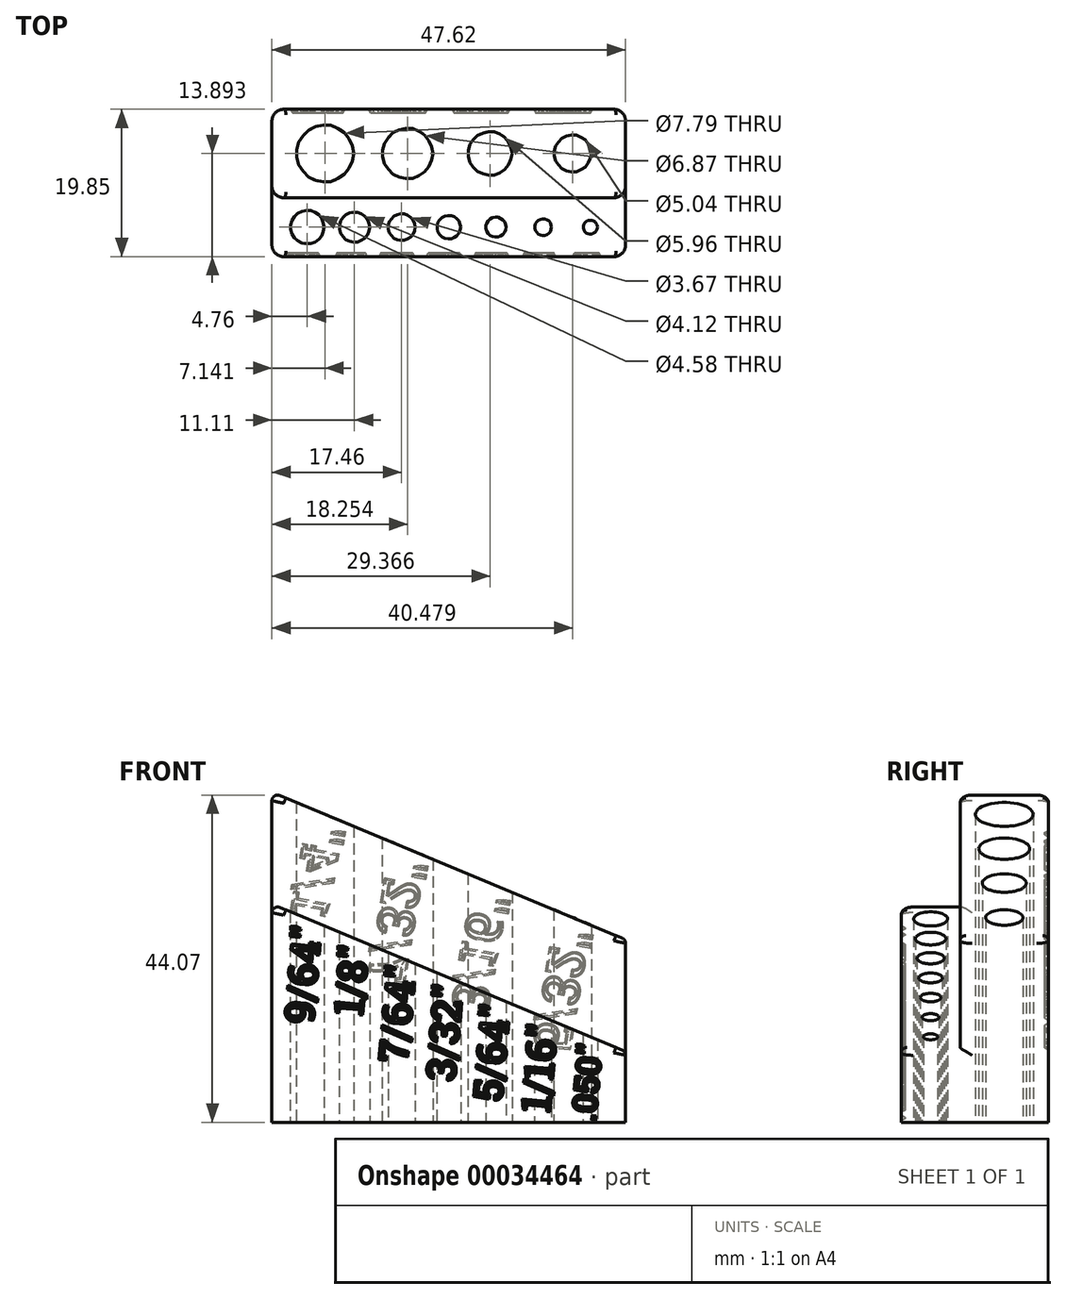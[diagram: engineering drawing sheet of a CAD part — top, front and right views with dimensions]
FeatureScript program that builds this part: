
annotation { "Feature Type Name" : "Feature", "Feature Type Description" : "" }
export const myFeature = defineFeature(function(context is Context, id is Id, definition is map)
    precondition{}
    {
        {
            var Q0;
            Q0=qCreatedBy(makeId("Front.planeOp"),FACE);
            var sketch = newSketch(context, id + "F0", { "sketchPlane" : qUnion([Q0])});
            skLineSegment(sketch, "E0", {"start": v(-23.81, 0) * mm, "end": v(23.81, 0) * mm});
            skLineSegment(sketch, "E1", {"start": v(23.81, 0) * mm, "end": v(23.81, 9.53) * mm});
            skLineSegment(sketch, "E2", {"start": v(23.81, 9.53) * mm, "end": v(-23.81, 29.37) * mm});
            skLineSegment(sketch, "E3", {"start": v(-23.81, 29.37) * mm, "end": v(-23.81, 0) * mm});
            skLineSegment(sketch, "E4", {"start": v(0, 0) * mm, "end": v(0, 19.45) * mm, "construction": true});
            skSolve(sketch);
        }
        {
            var Q0;
            Q0 = qSketchRegion(id + "F0", true);
            extrude(context, id + "F1", {"entities" : qUnion([Q0]), "depth" : 7.94 * mm});
        }
        {
            var Q0;
            Q0=qCreatedBy(makeId("Front.planeOp"),FACE);
            var sketch = newSketch(context, id + "F2", { "sketchPlane" : qUnion([Q0])});
            skLineSegment(sketch, "E5.0", {"start": v(-23.81, 0) * mm, "end": v(23.81, 0) * mm});
            skLineSegment(sketch, "E6", {"start": v(23.81, 0) * mm, "end": v(23.81, 24.6) * mm});
            skLineSegment(sketch, "E7", {"start": v(-23.81, 0) * mm, "end": v(-23.81, 44.45) * mm});
            skLineSegment(sketch, "E8", {"start": v(-23.81, 44.45) * mm, "end": v(23.81, 24.6) * mm});
            skLineSegment(sketch, "E9.0", {"start": v(23.81, 9.52) * mm, "end": v(-23.81, 29.37) * mm, "construction": true});
            skSolve(sketch);
        }
        {
            var Q0;
            Q0 = qSketchRegion(id + "F2", true);
            extrude(context, id + "F3", {"entities" : qUnion([Q0]), "operationType" : NewBodyOperationType.ADD, "oppositeDirection" : true, "depth" : 11.9 * mm});
        }
        {
            var Q0;
            Q0=qCreatedBy(makeId("Top.planeOp"),FACE);
            var sketch = newSketch(context, id + "F4", { "sketchPlane" : qUnion([Q0])});
            skLineSegment(sketch, "E10.0", {"start": v(23.81, 0) * mm, "end": v(-23.81, 0) * mm, "construction": true});
            skLineSegment(sketch, "E11.bottom", {"start": v(23.81, -7.94) * mm, "end": v(-23.81, -7.94) * mm, "construction": true});
            skLineSegment(sketch, "E11.top", {"start": v(23.81, 11.9) * mm, "end": v(-23.81, 11.9) * mm, "construction": true});
            skLineSegment(sketch, "E12", {"start": v(23.81, -3.97) * mm, "end": v(-23.81, -3.97) * mm, "construction": true});
            skLineSegment(sketch, "E13", {"start": v(23.81, -7.94) * mm, "end": v(23.81, 0) * mm, "construction": true});
            skLineSegment(sketch, "E14", {"start": v(-23.81, -7.94) * mm, "end": v(-23.81, 0) * mm, "construction": true});
            skLineSegment(sketch, "E15", {"start": v(-23.81, 11.9) * mm, "end": v(-23.81, 0) * mm, "construction": true});
            skLineSegment(sketch, "E16", {"start": v(23.81, 0) * mm, "end": v(23.81, 11.9) * mm, "construction": true});
            skCircle(sketch, "E17", {"center": v(19.05, -3.97) * mm, "radius": 0.73 * mm, "construction": true});
            skLineSegment(sketch, "E18", {"start": v(19.68, -4.34) * mm, "end": v(19.68, -3.6) * mm, "construction": true});
            skLineSegment(sketch, "E19", {"start": v(19.68, -3.6) * mm, "end": v(19.05, -3.24) * mm, "construction": true});
            skLineSegment(sketch, "E20", {"start": v(18.41, -4.34) * mm, "end": v(19.05, -4.7) * mm, "construction": true});
            skLineSegment(sketch, "E21", {"start": v(19.05, -4.7) * mm, "end": v(19.68, -4.34) * mm, "construction": true});
            skLineSegment(sketch, "E22", {"start": v(18.41, -4.34) * mm, "end": v(18.41, -3.6) * mm, "construction": true});
            skLineSegment(sketch, "E23", {"start": v(18.41, -3.6) * mm, "end": v(19.05, -3.24) * mm, "construction": true});
            skCircle(sketch, "E24", {"center": v(19.05, -3.97) * mm, "radius": 0.96 * mm});
            skLineSegment(sketch, "E25", {"start": v(19.05, -4.7) * mm, "end": v(19.05, -4.93) * mm, "construction": true});
            skCircle(sketch, "E26", {"center": v(12.7, -3.97) * mm, "radius": 0.92 * mm, "construction": true});
            skLineSegment(sketch, "E27", {"start": v(13.5, -4.43) * mm, "end": v(13.5, -3.51) * mm, "construction": true});
            skLineSegment(sketch, "E28", {"start": v(13.5, -3.51) * mm, "end": v(12.7, -3.05) * mm, "construction": true});
            skLineSegment(sketch, "E29", {"start": v(11.9, -4.43) * mm, "end": v(12.7, -4.89) * mm, "construction": true});
            skLineSegment(sketch, "E30", {"start": v(12.7, -4.89) * mm, "end": v(13.5, -4.43) * mm, "construction": true});
            skLineSegment(sketch, "E31", {"start": v(11.9, -4.43) * mm, "end": v(11.9, -3.51) * mm, "construction": true});
            skLineSegment(sketch, "E32", {"start": v(11.9, -3.51) * mm, "end": v(12.7, -3.05) * mm, "construction": true});
            skCircle(sketch, "E33", {"center": v(12.7, -3.97) * mm, "radius": 1.15 * mm});
            skLineSegment(sketch, "E34", {"start": v(12.7, -4.89) * mm, "end": v(12.7, -5.11) * mm, "construction": true});
            skCircle(sketch, "E35", {"center": v(6.35, -3.97) * mm, "radius": 1.15 * mm, "construction": true});
            skLineSegment(sketch, "E36", {"start": v(7.34, -4.54) * mm, "end": v(7.34, -3.4) * mm, "construction": true});
            skLineSegment(sketch, "E37", {"start": v(7.34, -3.4) * mm, "end": v(6.35, -2.82) * mm, "construction": true});
            skLineSegment(sketch, "E38", {"start": v(5.36, -4.54) * mm, "end": v(6.35, -5.11) * mm, "construction": true});
            skLineSegment(sketch, "E39", {"start": v(6.35, -5.11) * mm, "end": v(7.34, -4.54) * mm, "construction": true});
            skLineSegment(sketch, "E40", {"start": v(5.36, -4.54) * mm, "end": v(5.36, -3.4) * mm, "construction": true});
            skLineSegment(sketch, "E41", {"start": v(5.36, -3.4) * mm, "end": v(6.35, -2.82) * mm, "construction": true});
            skCircle(sketch, "E42", {"center": v(6.35, -3.97) * mm, "radius": 1.37 * mm});
            skLineSegment(sketch, "E43", {"start": v(6.35, -5.11) * mm, "end": v(6.35, -5.34) * mm, "construction": true});
            skCircle(sketch, "E44", {"center": v(0, -3.97) * mm, "radius": 1.37 * mm, "construction": true});
            skLineSegment(sketch, "E45", {"start": v(1.2, -4.66) * mm, "end": v(1.2, -3.28) * mm, "construction": true});
            skLineSegment(sketch, "E46", {"start": v(1.2, -3.28) * mm, "end": v(0, -2.6) * mm, "construction": true});
            skLineSegment(sketch, "E47", {"start": v(-1.2, -4.66) * mm, "end": v(0, -5.34) * mm, "construction": true});
            skLineSegment(sketch, "E48", {"start": v(0, -5.34) * mm, "end": v(1.2, -4.66) * mm, "construction": true});
            skLineSegment(sketch, "E49", {"start": v(-1.2, -4.66) * mm, "end": v(-1.2, -3.28) * mm, "construction": true});
            skLineSegment(sketch, "E50", {"start": v(-1.2, -3.28) * mm, "end": v(0, -2.6) * mm, "construction": true});
            skCircle(sketch, "E51", {"center": v(0, -3.97) * mm, "radius": 1.6 * mm});
            skLineSegment(sketch, "E52", {"start": v(0, -5.34) * mm, "end": v(0, -5.57) * mm, "construction": true});
            skCircle(sketch, "E53", {"center": v(-6.35, -3.97) * mm, "radius": 1.6 * mm, "construction": true});
            skLineSegment(sketch, "E54", {"start": v(-4.96, -4.77) * mm, "end": v(-4.96, -3.17) * mm, "construction": true});
            skLineSegment(sketch, "E55", {"start": v(-4.96, -3.17) * mm, "end": v(-6.35, -2.36) * mm, "construction": true});
            skLineSegment(sketch, "E56", {"start": v(-7.74, -4.77) * mm, "end": v(-6.35, -5.57) * mm, "construction": true});
            skLineSegment(sketch, "E57", {"start": v(-6.35, -5.57) * mm, "end": v(-4.96, -4.77) * mm, "construction": true});
            skLineSegment(sketch, "E58", {"start": v(-7.74, -4.77) * mm, "end": v(-7.74, -3.17) * mm, "construction": true});
            skLineSegment(sketch, "E59", {"start": v(-7.74, -3.17) * mm, "end": v(-6.35, -2.36) * mm, "construction": true});
            skCircle(sketch, "E60", {"center": v(-6.35, -3.97) * mm, "radius": 1.83 * mm});
            skLineSegment(sketch, "E61", {"start": v(-6.35, -5.57) * mm, "end": v(-6.35, -5.8) * mm, "construction": true});
            skCircle(sketch, "E62", {"center": v(-12.7, -3.97) * mm, "radius": 1.83 * mm, "construction": true});
            skLineSegment(sketch, "E63", {"start": v(-11.11, -4.89) * mm, "end": v(-11.11, -3.05) * mm, "construction": true});
            skLineSegment(sketch, "E64", {"start": v(-11.11, -3.05) * mm, "end": v(-12.7, -2.14) * mm, "construction": true});
            skLineSegment(sketch, "E65", {"start": v(-14.29, -4.89) * mm, "end": v(-12.7, -5.8) * mm, "construction": true});
            skLineSegment(sketch, "E66", {"start": v(-12.7, -5.8) * mm, "end": v(-11.11, -4.89) * mm, "construction": true});
            skLineSegment(sketch, "E67", {"start": v(-14.29, -4.89) * mm, "end": v(-14.29, -3.05) * mm, "construction": true});
            skLineSegment(sketch, "E68", {"start": v(-14.29, -3.05) * mm, "end": v(-12.7, -2.14) * mm, "construction": true});
            skCircle(sketch, "E69", {"center": v(-12.7, -3.97) * mm, "radius": 2.06 * mm});
            skLineSegment(sketch, "E70", {"start": v(-12.7, -5.8) * mm, "end": v(-12.7, -6.03) * mm, "construction": true});
            skCircle(sketch, "E71", {"center": v(-19.05, -3.97) * mm, "radius": 2.06 * mm, "construction": true});
            skLineSegment(sketch, "E72", {"start": v(-17.26, -5) * mm, "end": v(-17.26, -2.94) * mm, "construction": true});
            skLineSegment(sketch, "E73", {"start": v(-17.26, -2.94) * mm, "end": v(-19.05, -1.9) * mm, "construction": true});
            skLineSegment(sketch, "E74", {"start": v(-20.84, -5) * mm, "end": v(-19.05, -6.03) * mm, "construction": true});
            skLineSegment(sketch, "E75", {"start": v(-19.05, -6.03) * mm, "end": v(-17.26, -5) * mm, "construction": true});
            skLineSegment(sketch, "E76", {"start": v(-20.84, -5) * mm, "end": v(-20.84, -2.94) * mm, "construction": true});
            skLineSegment(sketch, "E77", {"start": v(-20.84, -2.94) * mm, "end": v(-19.05, -1.9) * mm, "construction": true});
            skCircle(sketch, "E78", {"center": v(-19.05, -3.97) * mm, "radius": 2.3 * mm});
            skLineSegment(sketch, "E79", {"start": v(-19.05, -6.03) * mm, "end": v(-19.05, -6.26) * mm, "construction": true});
            skCircle(sketch, "E80", {"center": v(16.67, 5.95) * mm, "radius": 2.3 * mm, "construction": true});
            skLineSegment(sketch, "E81", {"start": v(18.65, 4.8) * mm, "end": v(18.65, 7.1) * mm, "construction": true});
            skLineSegment(sketch, "E82", {"start": v(18.65, 7.1) * mm, "end": v(16.67, 8.24) * mm, "construction": true});
            skLineSegment(sketch, "E83", {"start": v(14.68, 4.8) * mm, "end": v(16.67, 3.66) * mm, "construction": true});
            skLineSegment(sketch, "E84", {"start": v(18.65, 4.8) * mm, "end": v(16.67, 3.66) * mm, "construction": true});
            skLineSegment(sketch, "E85", {"start": v(14.68, 4.8) * mm, "end": v(14.68, 7.1) * mm, "construction": true});
            skLineSegment(sketch, "E86", {"start": v(16.67, 8.24) * mm, "end": v(14.68, 7.1) * mm, "construction": true});
            skCircle(sketch, "E87", {"center": v(16.67, 5.95) * mm, "radius": 2.52 * mm});
            skLineSegment(sketch, "E88", {"start": v(16.67, 3.66) * mm, "end": v(16.67, 3.43) * mm, "construction": true});
            skCircle(sketch, "E89", {"center": v(5.56, 5.95) * mm, "radius": 2.75 * mm, "construction": true});
            skLineSegment(sketch, "E90", {"start": v(7.94, 4.58) * mm, "end": v(7.94, 7.33) * mm, "construction": true});
            skLineSegment(sketch, "E91", {"start": v(7.94, 7.33) * mm, "end": v(5.56, 8.7) * mm, "construction": true});
            skLineSegment(sketch, "E92", {"start": v(3.17, 4.58) * mm, "end": v(5.56, 3.2) * mm, "construction": true});
            skLineSegment(sketch, "E93", {"start": v(7.94, 4.58) * mm, "end": v(5.56, 3.2) * mm, "construction": true});
            skLineSegment(sketch, "E94", {"start": v(3.17, 4.58) * mm, "end": v(3.17, 7.33) * mm, "construction": true});
            skLineSegment(sketch, "E95", {"start": v(5.56, 8.7) * mm, "end": v(3.17, 7.33) * mm, "construction": true});
            skCircle(sketch, "E96", {"center": v(5.56, 5.95) * mm, "radius": 2.98 * mm});
            skLineSegment(sketch, "E97", {"start": v(5.56, 3.2) * mm, "end": v(5.56, 2.97) * mm, "construction": true});
            skCircle(sketch, "E98", {"center": v(-5.56, 5.95) * mm, "radius": 3.2 * mm, "construction": true});
            skLineSegment(sketch, "E99", {"start": v(-2.78, 4.35) * mm, "end": v(-2.78, 7.56) * mm, "construction": true});
            skLineSegment(sketch, "E100", {"start": v(-2.78, 7.56) * mm, "end": v(-5.56, 9.16) * mm, "construction": true});
            skLineSegment(sketch, "E101", {"start": v(-8.33, 4.35) * mm, "end": v(-5.56, 2.75) * mm, "construction": true});
            skLineSegment(sketch, "E102", {"start": v(-2.78, 4.35) * mm, "end": v(-5.56, 2.75) * mm, "construction": true});
            skLineSegment(sketch, "E103", {"start": v(-8.33, 4.35) * mm, "end": v(-8.33, 7.56) * mm, "construction": true});
            skLineSegment(sketch, "E104", {"start": v(-5.56, 9.16) * mm, "end": v(-8.33, 7.56) * mm, "construction": true});
            skCircle(sketch, "E105", {"center": v(-5.56, 5.95) * mm, "radius": 3.44 * mm});
            skLineSegment(sketch, "E106", {"start": v(-5.56, 2.75) * mm, "end": v(-5.56, 2.52) * mm, "construction": true});
            skCircle(sketch, "E107", {"center": v(-16.67, 5.95) * mm, "radius": 3.67 * mm, "construction": true});
            skLineSegment(sketch, "E108", {"start": v(-13.5, 4.12) * mm, "end": v(-13.5, 7.79) * mm, "construction": true});
            skLineSegment(sketch, "E109", {"start": v(-13.5, 7.79) * mm, "end": v(-16.67, 9.62) * mm, "construction": true});
            skLineSegment(sketch, "E110", {"start": v(-19.84, 4.12) * mm, "end": v(-16.67, 2.29) * mm, "construction": true});
            skLineSegment(sketch, "E111", {"start": v(-13.5, 4.12) * mm, "end": v(-16.67, 2.29) * mm, "construction": true});
            skLineSegment(sketch, "E112", {"start": v(-19.84, 4.12) * mm, "end": v(-19.84, 7.79) * mm, "construction": true});
            skLineSegment(sketch, "E113", {"start": v(-16.67, 9.62) * mm, "end": v(-19.84, 7.79) * mm, "construction": true});
            skCircle(sketch, "E114", {"center": v(-16.67, 5.95) * mm, "radius": 3.9 * mm});
            skLineSegment(sketch, "E115", {"start": v(-16.67, 2.29) * mm, "end": v(-16.67, 2.06) * mm, "construction": true});
            skLineSegment(sketch, "E116", {"start": v(-23.81, 5.95) * mm, "end": v(-16.67, 5.95) * mm, "construction": true});
            skLineSegment(sketch, "E117", {"start": v(-5.56, 5.95) * mm, "end": v(5.56, 5.95) * mm, "construction": true});
            skLineSegment(sketch, "E118", {"start": v(16.67, 5.95) * mm, "end": v(23.81, 5.95) * mm, "construction": true});
            skLineSegment(sketch, "E119", {"start": v(5.56, 5.95) * mm, "end": v(16.67, 5.95) * mm, "construction": true});
            skLineSegment(sketch, "E120", {"start": v(-5.56, 5.95) * mm, "end": v(-16.67, 5.95) * mm, "construction": true});
            skSolve(sketch);
        }
        {
            var Q0;
            Q0 = qSketchRegion(id + "F4", true);
            extrude(context, id + "F5", {"entities" : qUnion([Q0]), "operationType" : NewBodyOperationType.REMOVE, "endBound" : BoundingType.THROUGH_ALL, "depth" : 25.4 * mm});
        }
        {
            var Q0;
            Q0=makeQuery(id+"F1.opExtrude","CAP_EDGE",EDGE,{"disambiguationData":[OSD([sQuery(id+"F0.wireOp",EDGE,"E1")])],"isStart":false});
            var Q1;
            Q1=makeQuery(id+"F3.opExtrude","CAP_EDGE",EDGE,{"disambiguationData":[OSD([sQuery(id+"F2.wireOp",EDGE,"E6")])],"isStart":true});
            var Q2;
            Q2=makeQuery(id+"F3.opExtrude","CAP_EDGE",EDGE,{"disambiguationData":[OSD([sQuery(id+"F2.wireOp",EDGE,"E6")])],"isStart":false});
            var Q3;
            Q3=makeQuery(id+"F3.opExtrude","CAP_EDGE",EDGE,{"disambiguationData":[OSD([sQuery(id+"F2.wireOp",EDGE,"E7")])],"isStart":true});
            var Q4;
            Q4=makeQuery(id+"F3.opExtrude","CAP_EDGE",EDGE,{"disambiguationData":[OSD([sQuery(id+"F2.wireOp",EDGE,"E7")])],"isStart":false});
            var Q5;
            Q5=makeQuery(id+"F1.opExtrude","CAP_EDGE",EDGE,{"disambiguationData":[OSD([sQuery(id+"F0.wireOp",EDGE,"E3")])],"isStart":false});
            fillet(context, id + "F6", {"entities" : qUnion([Q0, Q1, Q2, Q3, Q4, Q5]), "radius" : 1.59 * mm, "tangentPropagation" : true, "allowEdgeOverflow" : false});
        }
        {
            var Q0;
            Q0=makeQuery(id+"F1.opExtrude","CAP_EDGE",EDGE,{"disambiguationData":[OSD([sQuery(id+"F0.wireOp",EDGE,"E2")])],"isStart":false});
            var Q1;
            Q1=makeQuery(id+"F3.opExtrude","CAP_EDGE",EDGE,{"disambiguationData":[OSD([sQuery(id+"F2.wireOp",EDGE,"E8")])],"isStart":true});
            fillet(context, id + "F7", {"entities" : qUnion([Q0, Q1]), "radius" : 0.76 * mm, "tangentPropagation" : true, "allowEdgeOverflow" : false});
        }
        {
            var Q0;
            Q0=makeQuery(id+"F1.opExtrude","CAP_FACE",FACE,{"disambiguationData":[OSD([sQuery(id+"F0.wireOp",EDGE,"E0"),sQuery(id+"F0.wireOp",EDGE,"E1"),sQuery(id+"F0.wireOp",EDGE,"E2"),sQuery(id+"F0.wireOp",EDGE,"E3")])],"isStart":false});
            var sketch = newSketch(context, id + "F8", { "sketchPlane" : qUnion([Q0])});
            skText(sketch, "E121", { "text": ".050\"", "fontName": "RobotoSlab-Bold.ttf"});
            skText(sketch, "E122", { "text": "1/16\"", "fontName": "RobotoSlab-Bold.ttf"});
            skLineSegment(sketch, "E123.0", {"start": v(11.55, 0) * mm, "end": v(13.85, 0) * mm});
            skLineSegment(sketch, "E123.1", {"start": v(4.98, 0) * mm, "end": v(7.72, 0) * mm, "construction": true});
            skLineSegment(sketch, "E123.2", {"start": v(-1.6, 0) * mm, "end": v(1.6, 0) * mm, "construction": true});
            skLineSegment(sketch, "E123.3", {"start": v(-8.18, 0) * mm, "end": v(-4.52, 0) * mm, "construction": true});
            skLineSegment(sketch, "E123.4", {"start": v(-14.76, 0) * mm, "end": v(-10.64, 0) * mm, "construction": true});
            skLineSegment(sketch, "E123.5", {"start": v(-21.34, 0) * mm, "end": v(-16.76, 0) * mm, "construction": true});
            skText(sketch, "E124", { "text": "5/64\"", "fontName": "RobotoSlab-Bold.ttf"});
            skText(sketch, "E125", { "text": "3/32\"", "fontName": "RobotoSlab-Bold.ttf"});
            skLineSegment(sketch, "E126.0", {"start": v(18.09, 11.91) * mm, "end": v(20.01, 11.1) * mm, "construction": true});
            skLineSegment(sketch, "E126.1", {"start": v(11.55, 14.63) * mm, "end": v(13.85, 13.68) * mm, "construction": true});
            skLineSegment(sketch, "E126.2", {"start": v(4.98, 17.37) * mm, "end": v(7.72, 16.23) * mm, "construction": true});
            skLineSegment(sketch, "E126.3", {"start": v(-1.6, 20.11) * mm, "end": v(1.6, 18.78) * mm, "construction": true});
            skLineSegment(sketch, "E126.4", {"start": v(-8.18, 22.86) * mm, "end": v(-4.52, 21.33) * mm, "construction": true});
            skLineSegment(sketch, "E126.5", {"start": v(-14.76, 25.6) * mm, "end": v(-10.64, 23.88) * mm, "construction": true});
            skLineSegment(sketch, "E126.6", {"start": v(-21.34, 28.34) * mm, "end": v(-16.76, 26.43) * mm, "construction": true});
            skLineSegment(sketch, "E127", {"start": v(19.05, 11.5) * mm, "end": v(19.05, -2.35) * mm, "construction": true});
            skLineSegment(sketch, "E128", {"start": v(12.7, 14.16) * mm, "end": v(12.7, 1.87) * mm, "construction": true});
            skPoint(sketch, "E129", {"position": v(12.7, 13.33) * mm});
            skText(sketch, "E130", { "text": "7/64\"", "fontName": "RobotoSlab-Bold.ttf"});
            skText(sketch, "E131", { "text": "1/8\"", "fontName": "RobotoSlab-Bold.ttf"});
            skText(sketch, "E132", { "text": "9/64\"", "fontName": "RobotoSlab-Bold.ttf"});
            skPoint(sketch, "E133", {"position": v(19.05, 10.68) * mm});
            skLineSegment(sketch, "E134", {"start": v(6.35, 16.8) * mm, "end": v(6.35, 11.14) * mm, "construction": true});
            skPoint(sketch, "E135", {"position": v(6.35, 15.98) * mm});
            skLineSegment(sketch, "E136", {"start": v(0, 19.45) * mm, "end": v(0, 17.4) * mm, "construction": true});
            skPoint(sketch, "E137", {"position": v(0, 18.62) * mm});
            skPoint(sketch, "E138", {"position": v(-6.35, 21.27) * mm});
            skPoint(sketch, "E139", {"position": v(-12.7, 23.91) * mm});
            skPoint(sketch, "E140", {"position": v(-19.05, 26.56) * mm});
            skLineSegment(sketch, "E141", {"start": v(-6.35, 23.43) * mm, "end": v(-6.35, 22.1) * mm, "construction": true});
            skLineSegment(sketch, "E142", {"start": v(-12.7, 29.83) * mm, "end": v(-12.7, 24.74) * mm, "construction": true});
            skLineSegment(sketch, "E143", {"start": v(-19.05, 27.38) * mm, "end": v(-19.05, 24.02) * mm, "construction": true});
            const initialGuessF8  = {"E121": [0.01977, -6e-05, 0.08716, 0.9962, 0.0033], "E122": [0.01361, 0.0012, 0.08716, 0.9962, 0.00394], "E124": [0.00716, 0.00268, 0.08716, 0.9962, 0.00394], "E125": [0.00082, 0.00541, 0.08716, 0.9962, 0.00394], "E130": [-0.00554, 0.00793, 0.08716, 0.9962, 0.00394], "E131": [-0.01157, 0.01426, 0.08716, 0.9962, 0.00394], "E132": [-0.01825, 0.01313, 0.08716, 0.9962, 0.00394]};
            skSetInitialGuess(sketch, initialGuessF8);
            skSolve(sketch);
        }
        {
            var Q0;
            Q0 = qSketchRegion(id + "F8", true);
            extrude(context, id + "F9", {"entities" : qUnion([Q0]), "operationType" : NewBodyOperationType.REMOVE, "oppositeDirection" : true, "depth" : 0.5 * mm, "offsetDistance" : 25.4 * mm, "hasDraft" : true, "draftAngle" : 25 * degree, "draftPullDirection" : true});
        }
        {
            var Q0;
            Q0=makeQuery(id+"F3.opExtrude","CAP_FACE",FACE,{"disambiguationData":[OSD([sQuery(id+"F2.wireOp",EDGE,"E5.0"),sQuery(id+"F2.wireOp",EDGE,"E6"),sQuery(id+"F2.wireOp",EDGE,"E7"),sQuery(id+"F2.wireOp",EDGE,"E8")])],"isStart":false});
            var sketch = newSketch(context, id + "F10", { "sketchPlane" : qUnion([Q0])});
            skLineSegment(sketch, "E144.6", {"start": v(-20.7, 40.59) * mm, "end": v(-12.63, 37.22) * mm, "construction": true});
            skText(sketch, "E145", { "text": "5/32\"\n", "fontName": "RobotoSlab-Bold.ttf"});
            skPoint(sketch, "E146", {"position": v(-16.67, 26.16) * mm});
            skLineSegment(sketch, "E147", {"start": v(-16.67, 38.9) * mm, "end": v(-16.67, 36.27) * mm, "construction": true});
            skLineSegment(sketch, "E148.0", {"start": v(-14.15, 28.63) * mm, "end": v(-19.19, 26.53) * mm, "construction": true});
            skLineSegment(sketch, "E148.1", {"start": v(-2.58, 33.45) * mm, "end": v(-8.53, 30.97) * mm, "construction": true});
            skLineSegment(sketch, "E148.2", {"start": v(9, 38.28) * mm, "end": v(2.12, 35.41) * mm, "construction": true});
            skLineSegment(sketch, "E148.3", {"start": v(20.56, 43.1) * mm, "end": v(12.77, 39.85) * mm, "construction": true});
            skLineSegment(sketch, "E149", {"start": v(16.67, 41.47) * mm, "end": v(16.67, 33.72) * mm, "construction": true});
            skLineSegment(sketch, "E150", {"start": v(5.56, 36.84) * mm, "end": v(5.56, 30.45) * mm, "construction": true});
            skLineSegment(sketch, "E151", {"start": v(-5.56, 32.21) * mm, "end": v(-5.56, 25.1) * mm, "construction": true});
            skLineSegment(sketch, "E152", {"start": v(-16.67, 27.58) * mm, "end": v(-16.67, 20.26) * mm, "construction": true});
            skLineSegment(sketch, "E153.6", {"start": v(-7.85, 39.62) * mm, "end": v(-3.27, 37.71) * mm, "construction": true});
            skText(sketch, "E154", { "text": "3/16\"", "fontName": "RobotoSlab-Bold.ttf"});
            skPoint(sketch, "E155", {"position": v(-5.56, 30.79) * mm});
            skLineSegment(sketch, "E156", {"start": v(-5.56, 38.67) * mm, "end": v(-5.56, 35.3) * mm, "construction": true});
            skLineSegment(sketch, "E157", {"start": v(-1.84, 40.57) * mm, "end": v(-1.84, 34.06) * mm, "construction": true});
            skText(sketch, "E158", { "text": "7/32\"", "fontName": "RobotoSlab-Bold.ttf"});
            skPoint(sketch, "E159", {"position": v(5.56, 35.42) * mm});
            skLineSegment(sketch, "E160", {"start": v(-16.38, 46) * mm, "end": v(-16.38, 39.49) * mm, "construction": true});
            skText(sketch, "E161", { "text": "1/4\"", "fontName": "RobotoSlab-Bold.ttf"});
            skPoint(sketch, "E162", {"position": v(16.67, 40.05) * mm});
            const initialGuessF10  = {"E145": [-0.01125, 0.01003, -0.17365, 0.9848, 0.00508], "E154": [-0.00024, 0.01526, -0.17365, 0.9848, 0.00508], "E158": [0.01099, 0.01924, -0.17365, 0.9848, 0.00508], "E161": [0.02133, 0.02826, -0.17365, 0.9848, 0.00508]};
            skSetInitialGuess(sketch, initialGuessF10);
            skSolve(sketch);
        }
        {
            var Q0;
            Q0 = qSketchRegion(id + "F10", true);
            extrude(context, id + "F11", {"entities" : qUnion([Q0]), "operationType" : NewBodyOperationType.REMOVE, "oppositeDirection" : true, "depth" : 0.5 * mm, "offsetDistance" : 25.4 * mm, "hasDraft" : true, "draftAngle" : 25 * degree, "draftPullDirection" : true});
        }
    });
